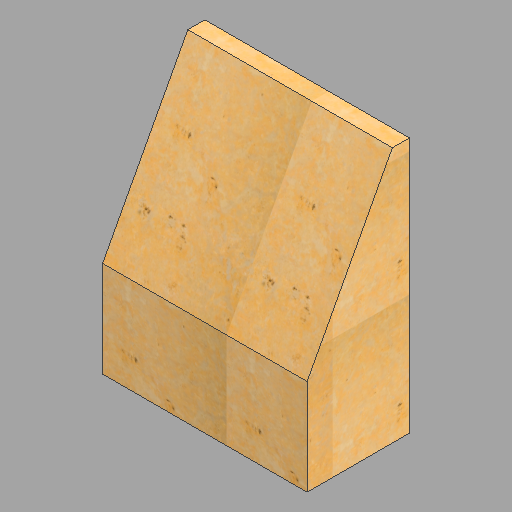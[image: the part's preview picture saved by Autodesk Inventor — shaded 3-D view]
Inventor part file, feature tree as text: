
AUTODESK INVENTOR PART (.ipt)
format: ipt  version: 2023 (Build 270158030, 158C)  size: 540,160 bytes
history: native  units: in
note: dims shown in document units (in); Inventor stores cm internally (conversion verified against a paired STEP export)
features: other x4, extrude x2, sketch x2
ambient origin geometry x8: Origin, YZ Plane, XZ Plane, XY Plane, X Axis, Y Axis, Z Axis, Center Point
bodies: Body1 (feature_tree)
feature tree (8):
  other  "Top"
  other  "Standard - Amber select"
  extrude  "Extrusion1"  Depth=0.3937in TaperAngle=0.0deg
  extrude  "Extrusion2"  Depth=12.5in
  other  "Top::Standard - Amber select"
  other  "TaggingFeature1"
  sketch  "Sketch1"  dims[d0=0.3937in d1=1.0in d2=0.0in]
  sketch  "Sketch2"  dims[d3=12.0in d4=8.0in d5=16.0in d6=16.0in d7=8.0in d8=1.5in d9=12.5in d10=0.0in]
